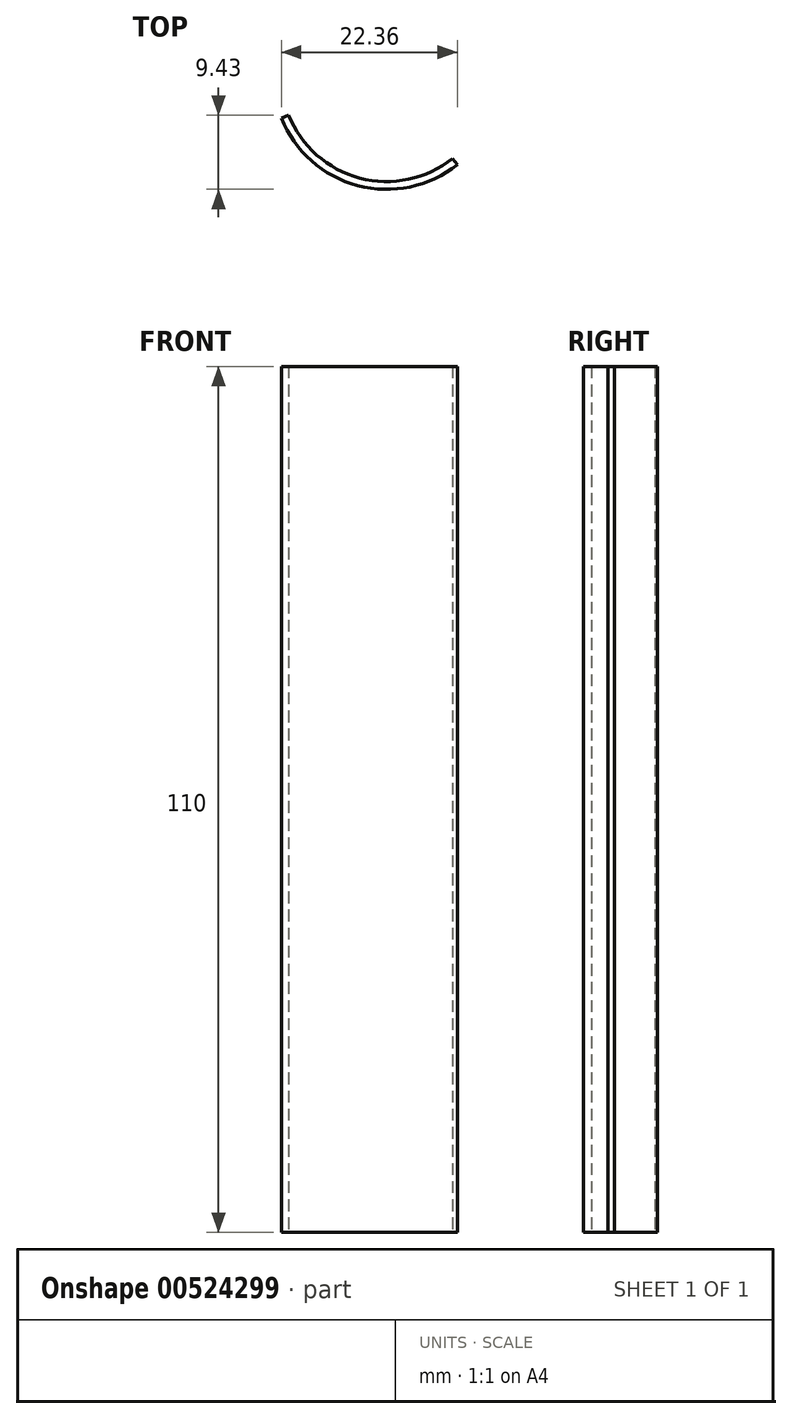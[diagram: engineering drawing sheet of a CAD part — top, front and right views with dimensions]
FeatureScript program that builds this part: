
annotation { "Feature Type Name" : "Feature", "Feature Type Description" : "" }
export const myFeature = defineFeature(function(context is Context, id is Id, definition is map)
    precondition{}
    {
        {
            var Q0;
            Q0=qCreatedBy(makeId("Top.planeOp"),FACE);
            var sketch = newSketch(context, id + "F0", { "sketchPlane" : qUnion([Q0])});
            skArc(sketch, "E0", {"start": v(-12.45, -4.97) * mm, "mid": v(-3.42, -12.96) * mm, "end": v(8.37, -10.47) * mm});
            skArc(sketch, "E1.0", {"start": v(-13.37, -5.34) * mm, "mid": v(-3.68, -13.92) * mm, "end": v(9, -11.25) * mm});
            skLineSegment(sketch, "E2", {"start": v(-13.37, -5.34) * mm, "end": v(-12.45, -4.97) * mm});
            skLineSegment(sketch, "E3", {"start": v(8.37, -10.47) * mm, "end": v(9, -11.25) * mm});
            skSolve(sketch);
        }
        {
            var Q0;
            Q0=makeQuery(id+"F0.imprint","IMPRINT",FACE,{"disambiguationData":[TD([[makeQuery(id+"F0.imprint","IMPRINT",EDGE,{"derivedFrom":sQuery(id+"F0.wireOp",EDGE,"E0")}),-1.0]])]});
            extrude(context, id + "F1", {"entities" : qUnion([Q0]), "depth" : 110 * mm, "offsetDistance" : 25.4 * mm});
        }
    });
